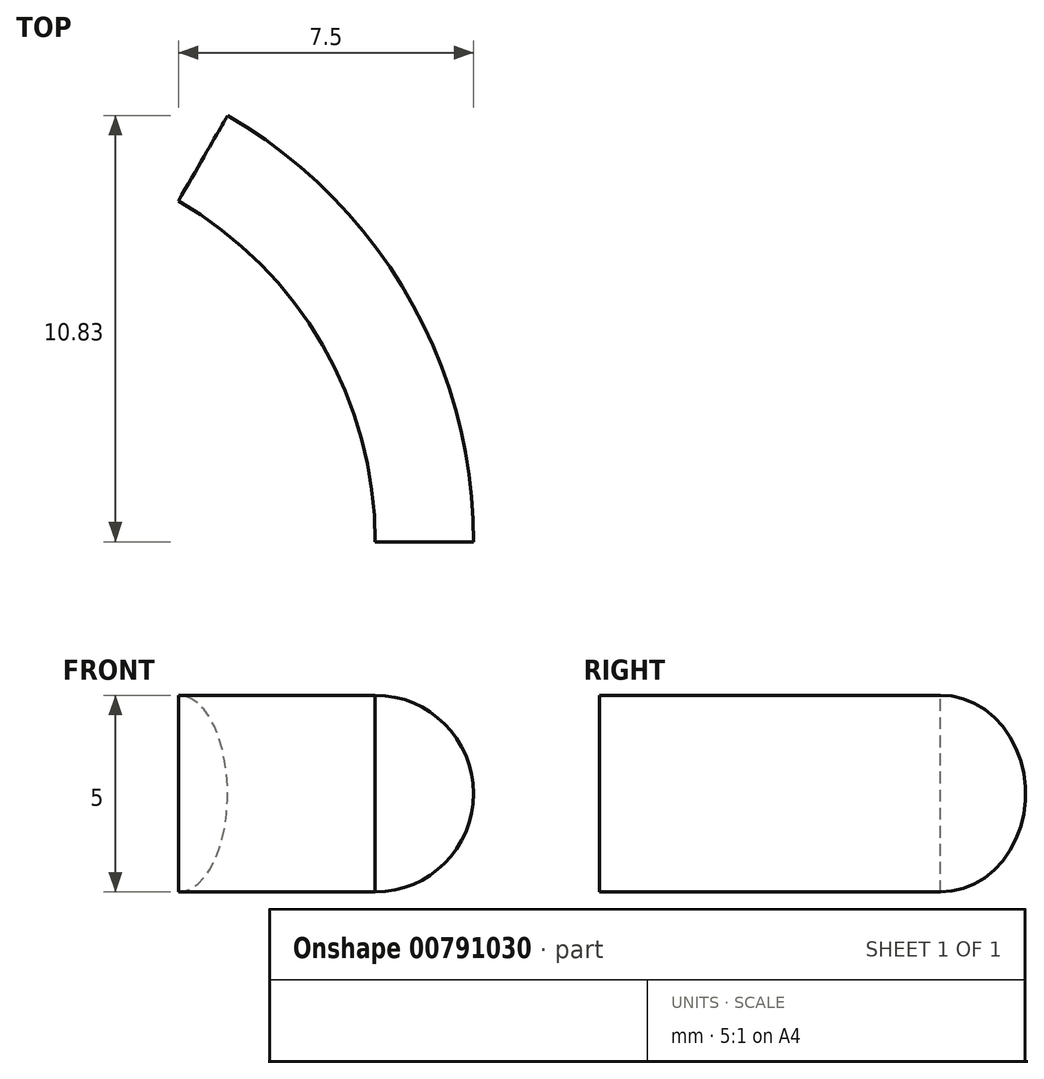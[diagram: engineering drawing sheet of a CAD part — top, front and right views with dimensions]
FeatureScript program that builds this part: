
annotation { "Feature Type Name" : "Feature", "Feature Type Description" : "" }
export const myFeature = defineFeature(function(context is Context, id is Id, definition is map)
    precondition{}
    {
        {
            var Q0;
            Q0=qCreatedBy(makeId("Front.planeOp"),FACE);
            var sketch = newSketch(context, id + "F0", { "sketchPlane" : qUnion([Q0])});
            skLineSegment(sketch, "E0", {"start": v(0, 0) * mm, "end": v(0, 5) * mm});
            skArc(sketch, "E1", {"start": v(0, 0) * mm, "mid": v(2.5, 2.5) * mm, "end": v(0, 5) * mm});
            skLineSegment(sketch, "E2", {"start": v(0, 0) * mm, "end": v(-10, 0) * mm});
            skLineSegment(sketch, "E3", {"start": v(-10, 0) * mm, "end": v(-10, 18.8) * mm});
            skSolve(sketch);
        }
        {
            var Q0;
            Q0 = qSketchRegion(id + "F0", true);
            var Q1;
            Q1=sQuery(id+"F0.wireOp",EDGE,"E3");
            revolve(context, id + "F1", {"surfaceOperationType" : NewSurfaceOperationType.NEW, "entities" : qUnion([Q0]), "axis" : qUnion([Q1]), "revolveType" : RevolveType.ONE_DIRECTION, "angle" : 60 * degree});
        }
    });
